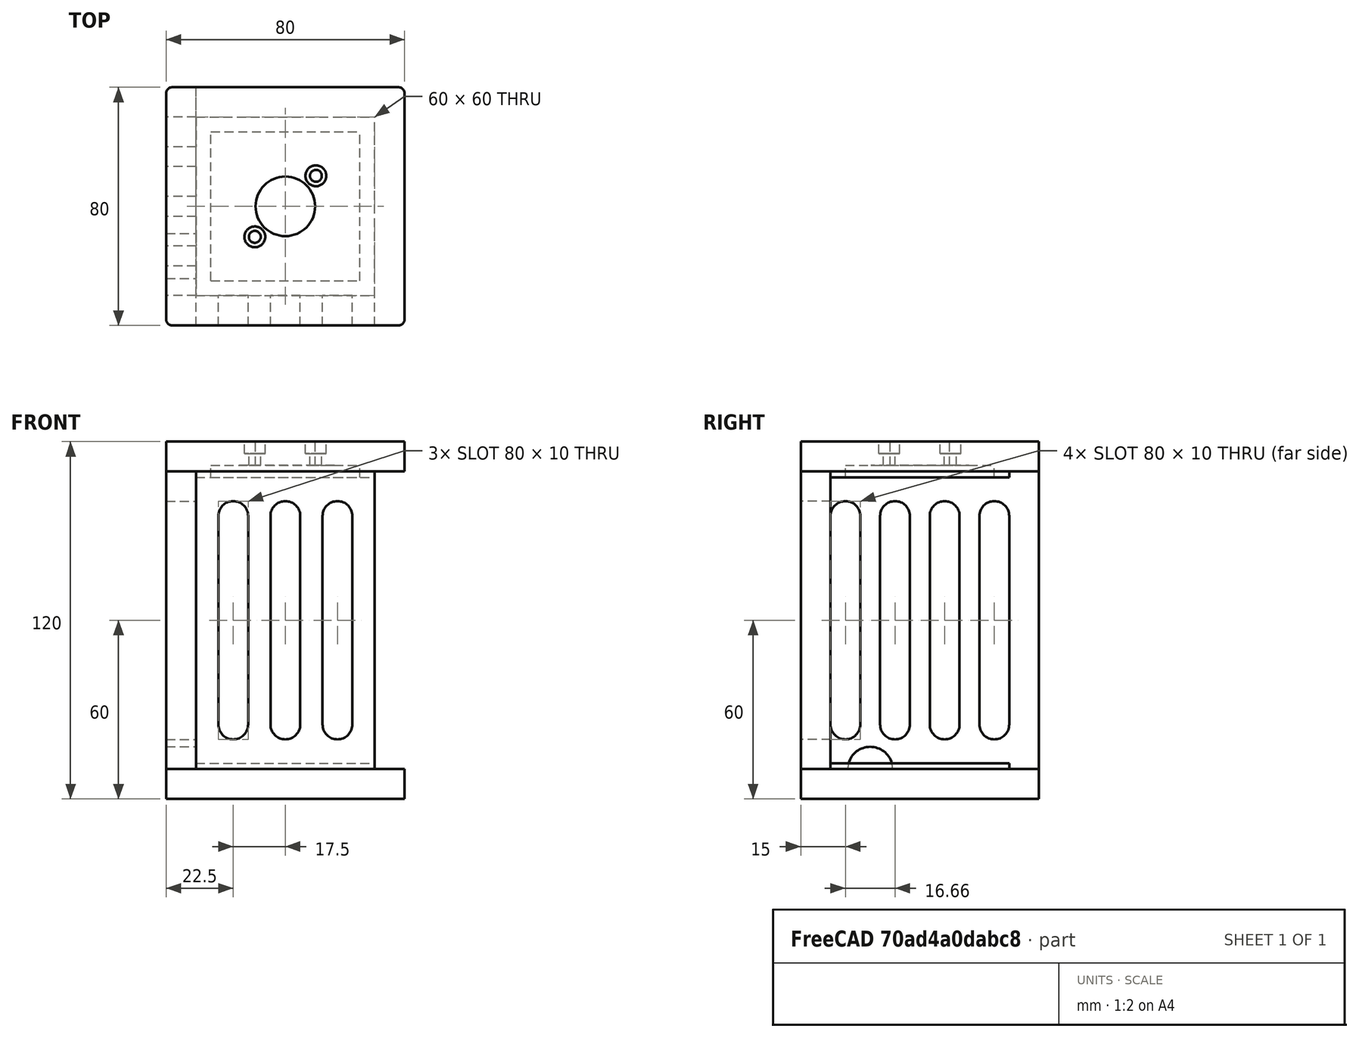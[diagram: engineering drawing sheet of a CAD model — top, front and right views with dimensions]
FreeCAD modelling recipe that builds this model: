
FCSTD DOCUMENT  (FreeCAD 0.19R24291 (Git))
Label: jaulita nueva
License: All rights reserved
LicenseURL: http://en.wikipedia.org/wiki/All_rights_reserved
objects: Part::Cylinder×28, Part::Cut×19, Part::Box×16, Part::MultiFuse×14, Part::Fillet×7
note: 84 computed .brp shape members not serialized (recipe doc carries the construction recipe); baked Part::Feature solids carry a one-line shape summary decoded from their .brp

FEATURE [Part::Box] Box  label="Cubo"
  AttacherType = Attacher::AttachEngine3D
  Height = 10
  Length = 80
  Width = 80
FEATURE [Part::Box] Box001  label="Cubo001"
  AttacherType = Attacher::AttachEngine3D
  Height = 100
  Length = 60
  Placement = pos=(10,0,10) rot=(0,0,1;0rad)
  Width = 10
FEATURE [Part::Box] Box002  label="Cubo002"
  AttacherType = Attacher::AttachEngine3D
  Height = 100
  Length = 10
  Placement = pos=(0,0,10) rot=(0,0,1;0rad)
  Width = 80
FEATURE [Part::Box] Box004  label="Cubo004"
  AttacherType = Attacher::AttachEngine3D
  Height = 2
  Length = 60
  Placement = pos=(10,10,10) rot=(0,0,1;0rad)
  Width = 60
FEATURE [Part::Box] Box005  label="Cubo005"
  AttacherType = Attacher::AttachEngine3D
  Height = 2
  Length = 60
  Placement = pos=(10,10,108) rot=(0,0,1;0rad)
  Width = 60
FEATURE [Part::Box] Box007  label="Cubo007"
  AttacherType = Attacher::AttachEngine3D
  Height = 70
  Length = 10
  Placement = pos=(10,0,25) rot=(0,0,1;0rad)
  Width = 10
FEATURE [Part::Cylinder] Cylinder  label="Cilindro"
  Angle = 360
  AttacherType = Attacher::AttachEngine3D
  Height = 10
  Placement = pos=(15,10,25) rot=(1,0,0;1.5708rad)
  Radius = 5
FEATURE [Part::Cylinder] Cylinder001  label="Cilindro001"
  Angle = 360
  AttacherType = Attacher::AttachEngine3D
  Height = 10
  Placement = pos=(15,10,95) rot=(1,0,0;1.5708rad)
  Radius = 5
FEATURE [Part::MultiFuse] Fusion
  Placement = pos=(7.5,0,0) rot=(0,0,1;0rad)
  Shapes = -> [Box007,Cylinder,Cylinder001]
FEATURE [Part::Cylinder] Cylinder002  label="Cilindro002"
  Angle = 360
  AttacherType = Attacher::AttachEngine3D
  Height = 10
  Placement = pos=(15,10,25) rot=(1,0,0;1.5708rad)
  Radius = 5
FEATURE [Part::Box] Box008  label="Cubo008"
  AttacherType = Attacher::AttachEngine3D
  Height = 70
  Length = 10
  Placement = pos=(10,0,25) rot=(0,0,1;0rad)
  Width = 10
FEATURE [Part::Cylinder] Cylinder003  label="Cilindro003"
  Angle = 360
  AttacherType = Attacher::AttachEngine3D
  Height = 10
  Placement = pos=(15,10,95) rot=(1,0,0;1.5708rad)
  Radius = 5
FEATURE [Part::MultiFuse] Fusion001
  Placement = pos=(25,0,0) rot=(0,0,1;0rad)
  Shapes = -> [Box008,Cylinder002,Cylinder003]
FEATURE [Part::Cylinder] Cylinder004  label="Cilindro004"
  Angle = 360
  AttacherType = Attacher::AttachEngine3D
  Height = 10
  Placement = pos=(15,10,25) rot=(1,0,0;1.5708rad)
  Radius = 5
FEATURE [Part::Box] Box009  label="Cubo009"
  AttacherType = Attacher::AttachEngine3D
  Height = 70
  Length = 10
  Placement = pos=(10,0,25) rot=(0,0,1;0rad)
  Width = 10
FEATURE [Part::Cylinder] Cylinder005  label="Cilindro005"
  Angle = 360
  AttacherType = Attacher::AttachEngine3D
  Height = 10
  Placement = pos=(15,10,95) rot=(1,0,0;1.5708rad)
  Radius = 5
FEATURE [Part::MultiFuse] Fusion002
  Placement = pos=(42.5,0,0) rot=(0,0,1;0rad)
  Shapes = -> [Box009,Cylinder004,Cylinder005]
FEATURE [Part::Cut] Cut001
  Base = -> Box001
  Tool = -> Fusion
FEATURE [Part::Cylinder] Cylinder006  label="Cilindro006"
  Angle = 360
  AttacherType = Attacher::AttachEngine3D
  Height = 10
  Placement = pos=(15,10,95) rot=(1,0,0;1.5708rad)
  Radius = 5
FEATURE [Part::Box] Box010  label="Cubo010"
  AttacherType = Attacher::AttachEngine3D
  Height = 70
  Length = 10
  Placement = pos=(10,0,25) rot=(0,0,1;0rad)
  Width = 10
FEATURE [Part::Cylinder] Cylinder007  label="Cilindro007"
  Angle = 360
  AttacherType = Attacher::AttachEngine3D
  Height = 10
  Placement = pos=(15,10,25) rot=(1,0,0;1.5708rad)
  Radius = 5
FEATURE [Part::MultiFuse] Fusion003
  Placement = pos=(10,0,0) rot=(0,0,1;1.5708rad)
  Shapes = -> [Box010,Cylinder007,Cylinder006]
FEATURE [Part::Box] Box011  label="Cubo011"
  AttacherType = Attacher::AttachEngine3D
  Height = 70
  Length = 10
  Placement = pos=(10,0,25) rot=(0,0,1;0rad)
  Width = 10
FEATURE [Part::Cylinder] Cylinder008  label="Cilindro008"
  Angle = 360
  AttacherType = Attacher::AttachEngine3D
  Height = 10
  Placement = pos=(15,10,25) rot=(1,0,0;1.5708rad)
  Radius = 5
FEATURE [Part::Cylinder] Cylinder009  label="Cilindro009"
  Angle = 360
  AttacherType = Attacher::AttachEngine3D
  Height = 10
  Placement = pos=(15,10,95) rot=(1,0,0;1.5708rad)
  Radius = 5
FEATURE [Part::MultiFuse] Fusion004
  Placement = pos=(10,16.66,0) rot=(0,0,1;1.5708rad)
  Shapes = -> [Box011,Cylinder008,Cylinder009]
FEATURE [Part::Box] Box012  label="Cubo012"
  AttacherType = Attacher::AttachEngine3D
  Height = 70
  Length = 10
  Placement = pos=(10,0,25) rot=(0,0,1;0rad)
  Width = 10
FEATURE [Part::Cylinder] Cylinder010  label="Cilindro010"
  Angle = 360
  AttacherType = Attacher::AttachEngine3D
  Height = 10
  Placement = pos=(15,10,25) rot=(1,0,0;1.5708rad)
  Radius = 5
FEATURE [Part::Cylinder] Cylinder011  label="Cilindro011"
  Angle = 360
  AttacherType = Attacher::AttachEngine3D
  Height = 10
  Placement = pos=(15,10,95) rot=(1,0,0;1.5708rad)
  Radius = 5
FEATURE [Part::MultiFuse] Fusion005
  Placement = pos=(10,33.33,0) rot=(0,0,1;1.5708rad)
  Shapes = -> [Box012,Cylinder010,Cylinder011]
FEATURE [Part::Box] Box013  label="Cubo013"
  AttacherType = Attacher::AttachEngine3D
  Height = 70
  Length = 10
  Placement = pos=(10,0,25) rot=(0,0,1;0rad)
  Width = 10
FEATURE [Part::Cylinder] Cylinder012  label="Cilindro012"
  Angle = 360
  AttacherType = Attacher::AttachEngine3D
  Height = 10
  Placement = pos=(15,10,25) rot=(1,0,0;1.5708rad)
  Radius = 5
FEATURE [Part::Cylinder] Cylinder013  label="Cilindro013"
  Angle = 360
  AttacherType = Attacher::AttachEngine3D
  Height = 10
  Placement = pos=(15,10,95) rot=(1,0,0;1.5708rad)
  Radius = 5
FEATURE [Part::MultiFuse] Fusion006
  Placement = pos=(10,50,0) rot=(0,0,1;1.5708rad)
  Shapes = -> [Box013,Cylinder012,Cylinder013]
FEATURE [Part::Cut] Cut
  Base = -> Box002
  Tool = -> Fusion006
FEATURE [Part::Cut] Cut004
  Base = -> Cut
  Tool = -> Fusion005
FEATURE [Part::Cut] Cut005
  Base = -> Cut004
  Tool = -> Fusion004
FEATURE [Part::Cut] Cut006
  Base = -> Cut005
  Tool = -> Fusion003
FEATURE [Part::Cylinder] Cylinder014  label="Cilindro014"
  Angle = 180
  AttacherType = Attacher::AttachEngine3D
  Height = 10
  Placement = pos=(0,23.33,10) rot=(0.57735,0.57735,0.57735;2.0944rad)
  Radius = 7.5
FEATURE [Part::Cut] Cut007
  Base = -> Cut006
  Tool = -> Cylinder014
FEATURE [Part::MultiFuse] Fusion008
  Shapes = -> [Box,Box004]
FEATURE [Part::Fillet] Fillet001
  Base = -> Cut007
  Edges = 1 edges r=2: [Edge6]
FEATURE [Part::Fillet] Fillet005
  Base = -> Fusion008
  Edges = 4 edges r=2: [Edge1,Edge3,Edge6,Edge15]
FEATURE [Part::Cylinder] Cylinder021  label="Cilindro021"
  Angle = 360
  AttacherType = Attacher::AttachEngine3D
  Height = 15
  Placement = pos=(40,40,106) rot=(0,0,1;0rad)
  Radius = 10
FEATURE [Part::Cylinder] Cylinder022  label="Cilindro022"
  Angle = 360
  AttacherType = Attacher::AttachEngine3D
  Height = 20
  Placement = pos=(54.5,54.5,105) rot=(0,0,1;0rad)
  Radius = 2
FEATURE [Part::Cylinder] Cylinder023  label="Cilindro023"
  Angle = 360
  AttacherType = Attacher::AttachEngine3D
  Height = 4
  Placement = pos=(25.5,25.5,116) rot=(0,0,1;0rad)
  Radius = 3.5
FEATURE [Part::Box] Box017  label="Cubo017"
  AttacherType = Attacher::AttachEngine3D
  Height = 10
  Length = 80
  Placement = pos=(0,0,110) rot=(0,0,1;0rad)
  Width = 80
FEATURE [Part::Cylinder] Cylinder024  label="Cilindro024"
  Angle = 360
  AttacherType = Attacher::AttachEngine3D
  Height = 20
  Placement = pos=(25.5,25.5,105) rot=(0,0,1;0rad)
  Radius = 2
FEATURE [Part::Box] Box018  label="Cubo018"
  AttacherType = Attacher::AttachEngine3D
  Height = 2
  Length = 60
  Placement = pos=(10,10,108) rot=(0,0,1;0rad)
  Width = 60
FEATURE [Part::MultiFuse] Fusion009
  Shapes = -> [Box017,Box018]
FEATURE [Part::Cut] Cut016
  Base = -> Fusion009
  Tool = -> Cylinder021
FEATURE [Part::Cut] Cut014
  Base = -> Cut016
  Tool = -> Cylinder022
FEATURE [Part::Cut] Cut013
  Base = -> Cut014
  Tool = -> Cylinder024
FEATURE [Part::Cut] Cut017
  Base = -> Cut013
  Tool = -> Cylinder023
FEATURE [Part::Cut] Cut018
  Base = -> Cut001
  Tool = -> Fusion002
FEATURE [Part::Cut] Cut019
  Base = -> Cut018
  Tool = -> Fusion001
FEATURE [Part::MultiFuse] Fusion010
  Shapes = -> [Cut017,Box005]
FEATURE [Part::Cylinder] Cylinder025  label="Cilindro025"
  Angle = 360
  AttacherType = Attacher::AttachEngine3D
  Height = 4
  Placement = pos=(54.5,54.5,116) rot=(0,0,1;0rad)
  Radius = 3.5
FEATURE [Part::Cut] Cut020
  Base = -> Fusion010
  Tool = -> Cylinder025
FEATURE [Part::Cylinder] Cylinder026  label="Cilindro026"
  Angle = 360
  AttacherType = Attacher::AttachEngine3D
  Height = 30
  Placement = pos=(54.5,54.5,95) rot=(0,0,1;0rad)
  Radius = 2
FEATURE [Part::Cylinder] Cylinder027  label="Cilindro027"
  Angle = 360
  AttacherType = Attacher::AttachEngine3D
  Height = 30
  Placement = pos=(25.5,25.5,95) rot=(0,0,1;0rad)
  Radius = 2
FEATURE [Part::Cut] Cut021
  Base = -> Cut020
  Tool = -> Cylinder026
FEATURE [Part::Cut] Cut022
  Base = -> Cut021
  Tool = -> Cylinder027
FEATURE [Part::Cylinder] Cylinder028  label="Cilindro028"
  Angle = 360
  AttacherType = Attacher::AttachEngine3D
  Height = 30
  Placement = pos=(40,40,95) rot=(0,0,1;0rad)
  Radius = 10
FEATURE [Part::Cut] Cut023
  Base = -> Cut022
  Tool = -> Cylinder028
FEATURE [Part::Fillet] Fillet006
  Base = -> Cut023
  Edges = 1 edges r=2: [Edge20]
FEATURE [Part::Fillet] Fillet007
  Base = -> Fillet006
  Edges = 1 edges r=2: [Edge18]
FEATURE [Part::Fillet] Fillet008
  Base = -> Fillet007
  Edges = 1 edges r=2: [Edge19]
FEATURE [Part::Fillet] Fillet009
  Base = -> Fillet008
  Edges = 1 edges r=2: [Edge19]
FEATURE [Part::Fillet] Fillet011
  Base = -> Fillet001
  Edges = 1 edges r=2: [Edge6]
FEATURE [Part::Box] Box019  label="Cubo019"
  AttacherType = Attacher::AttachEngine3D
  Height = 4
  Length = 50
  Placement = pos=(15,15,108) rot=(0,0,1;0rad)
  Width = 50
FEATURE [Part::Cut] Cut024
  Base = -> Fillet009
  Tool = -> Box019
FEATURE [Part::Box] Box020  label="Cubo020"
  AttacherType = Attacher::AttachEngine3D
  Height = 8
  Length = 60
  Placement = pos=(10,10,112) rot=(0,0,1;0rad)
  Width = 60
FEATURE [Part::MultiFuse] Fusion011
  Shapes = -> [Cut024,Box020]
FEATURE [Part::Cylinder] Cylinder029  label="Cilindro029"
  Angle = 360
  AttacherType = Attacher::AttachEngine3D
  Height = 20
  Placement = pos=(54.5,40,112) rot=(0,0,1;0rad)
  Radius = 2
FEATURE [Part::Cylinder] Cylinder032  label="Cilindro032"
  Angle = 360
  AttacherType = Attacher::AttachEngine3D
  Height = 20
  Placement = pos=(54.5,40,112) rot=(0,0,1;0rad)
  Radius = 2
FEATURE [Part::Cylinder] Cylinder030  label="Cilindro030"
  Angle = 360
  AttacherType = Attacher::AttachEngine3D
  Height = 4
  Placement = pos=(54.5,40,116) rot=(0,0,1;0rad)
  Radius = 3.5
FEATURE [Part::MultiFuse] Fusion012
  Shapes = -> [Cylinder029,Cylinder030]
FEATURE [Part::Cylinder] Cylinder031  label="Cilindro031"
  Angle = 360
  AttacherType = Attacher::AttachEngine3D
  Height = 4
  Placement = pos=(54.5,40,116) rot=(0,0,1;0rad)
  Radius = 3.5
FEATURE [Part::MultiFuse] Fusion013
  Placement = pos=(-29,0,0) rot=(0,0,1;0rad)
  Shapes = -> [Cylinder032,Cylinder031]
FEATURE [Part::MultiFuse] Fusion014
  Placement = pos=(40,-16.5685,0) rot=(0,0,1;0.785398rad)
  Shapes = -> [Fusion012,Fusion013]
FEATURE [Part::Cut] Cut025
  Base = -> Fusion011
  Tool = -> Fusion014
FEATURE [Part::Cylinder] Cylinder033  label="Cilindro033"
  Angle = 360
  AttacherType = Attacher::AttachEngine3D
  Height = 20
  Placement = pos=(40,40,105) rot=(0,0,1;0rad)
  Radius = 10
FEATURE [Part::Cut] Cut026
  Base = -> Cut025
  Tool = -> Cylinder033
